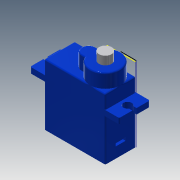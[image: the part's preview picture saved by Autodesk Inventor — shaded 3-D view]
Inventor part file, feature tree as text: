
AUTODESK INVENTOR PART (.ipt)
format: ipt  version: 2021 (Build 250183000, 183)  size: 254,464 bytes
history: native  units: mm
features: sketch x6, extrude x5, other x2, fillet x1
ambient origin geometry x8: Origin, YZ Plane, XZ Plane, XY Plane, X Axis, Y Axis, Z Axis, Center Point
bodies: Body1 (feature_tree)
feature tree (14):
  other  "솔리드1"
  extrude  "돌출1"  Depth=11.0mm
  other  "작업 평면1"
  extrude  "돌출2"  Depth=22.0mm TaperAngle=0.0deg
  extrude  "돌출3"  [1 undecoded]
  fillet  "모깎기1"  Radius=5.0mm
  extrude  "돌출4"  Depth=5.0mm
  extrude  "돌출6"  Depth=3.0mm
  sketch  "Esboço7"  dims[d0=22.0mm d1=11.0mm d2=22.0mm d3=0.0mm d4=-15.0mm d5=5.0mm d6=5.0mm d7=3.0mm d8=2.5mm d9=1.5mm d10=2.0mm d11=0.0mm d12=6.0mm d13=5.0mm d14=5.0mm d15=0.0mm d16=0.5mm d17=4.5mm d18=3.0mm d19=0.0mm d25=1.2mm d26=3.6mm d27=5.0mm d28=1.0mm d29=0.0mm]
  sketch  "스케치1"
  sketch  "스케치2"
  sketch  "스케치3"
  sketch  "스케치4"
  sketch  "스케치6"
note: 1 required parameter value undecoded (feature->parameter linkage not recoverable at this tier; creation-order binding heuristic only, values carry confidence <= 0.55)
